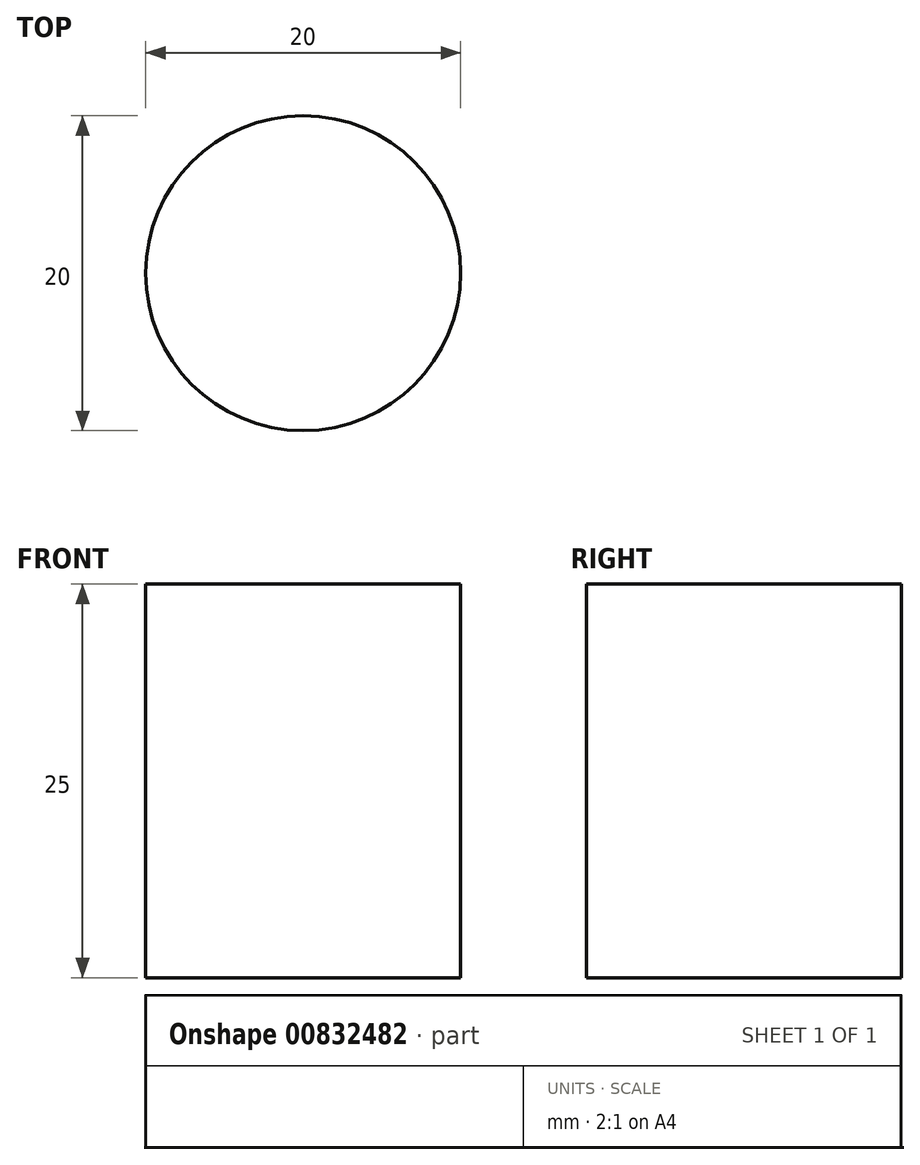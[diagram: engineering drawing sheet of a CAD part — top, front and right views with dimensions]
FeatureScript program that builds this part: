
annotation { "Feature Type Name" : "Feature", "Feature Type Description" : "" }
export const myFeature = defineFeature(function(context is Context, id is Id, definition is map)
    precondition{}
    {
        {
            var Q0;
            Q0=qCreatedBy(makeId("Top.planeOp"),FACE);
            var sketch = newSketch(context, id + "F0", { "sketchPlane" : qUnion([Q0])});
            skCircle(sketch, "E0", {"center": v(0, 0) * mm, "radius": 10 * mm});
            skSolve(sketch);
        }
        {
            var Q0;
            Q0=makeQuery(id+"F0.imprint","IMPRINT",FACE,{"disambiguationData":[TD([[makeQuery(id+"F0.imprint","IMPRINT",EDGE,{"derivedFrom":sQuery(id+"F0.wireOp",EDGE,"E0")}),1.0]])]});
            extrude(context, id + "F1", {"entities" : qUnion([Q0]), "depth" : 25 * mm, "offsetDistance" : 25 * mm});
        }
    });
